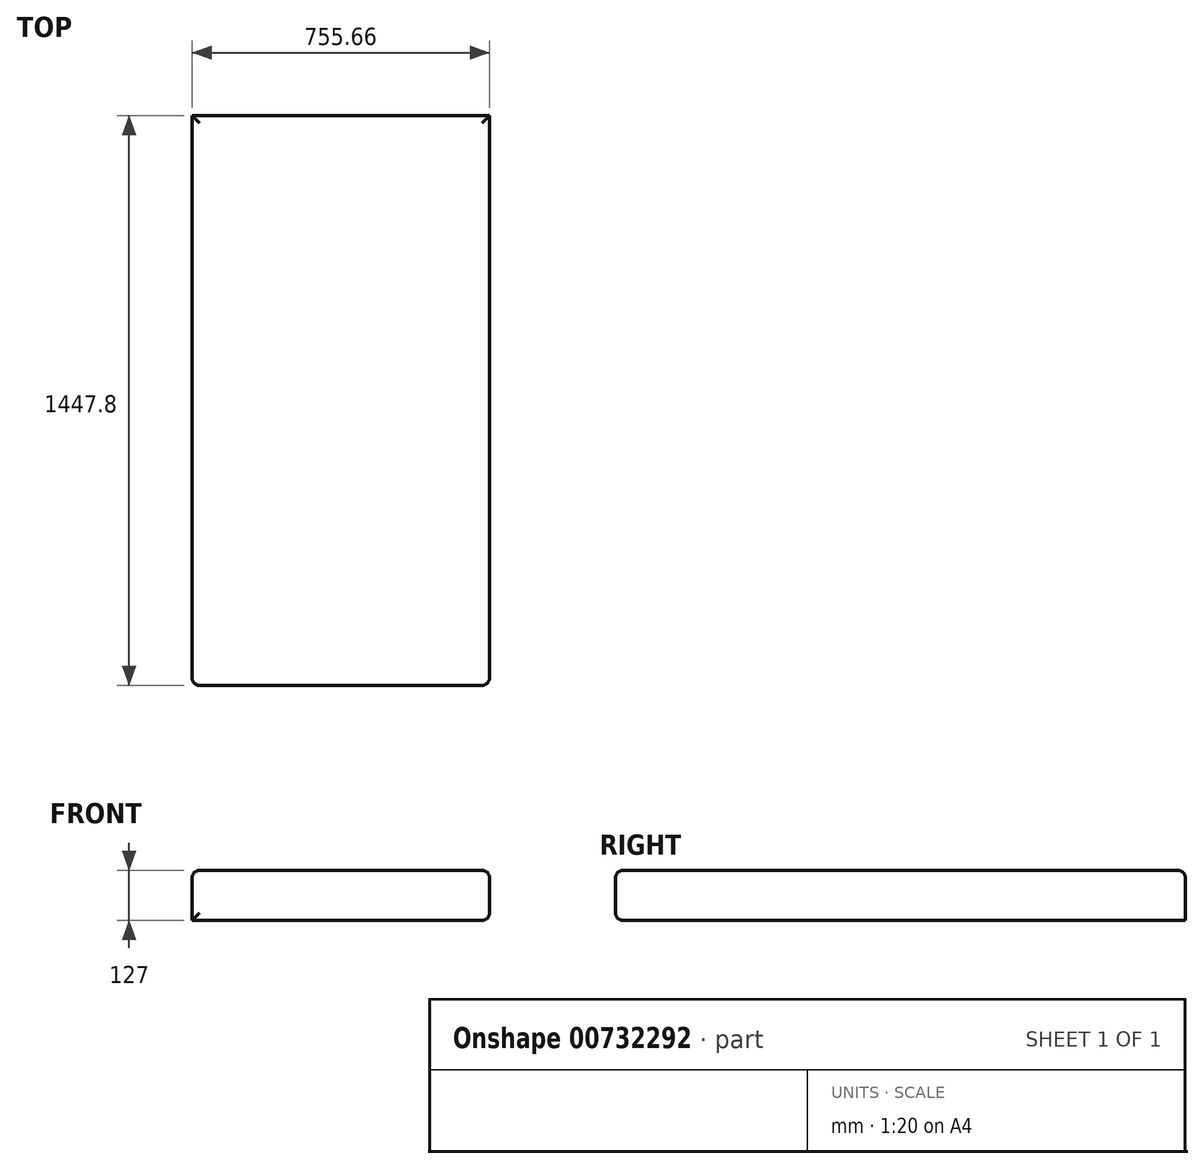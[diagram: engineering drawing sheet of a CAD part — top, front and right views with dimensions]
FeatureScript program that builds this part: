
annotation { "Feature Type Name" : "Feature", "Feature Type Description" : "" }
export const myFeature = defineFeature(function(context is Context, id is Id, definition is map)
    precondition{}
    {
        {
            var Q0;
            Q0=qCreatedBy(makeId("Top.planeOp"),FACE);
            var sketch = newSketch(context, id + "F0", { "sketchPlane" : qUnion([Q0])});
            skLineSegment(sketch, "E0.bottom", {"start": v(377.83, 723.9) * mm, "end": v(-377.83, 723.9) * mm});
            skLineSegment(sketch, "E0.top", {"start": v(377.82, -723.9) * mm, "end": v(-377.83, -723.9) * mm});
            skLineSegment(sketch, "E0.left", {"start": v(377.83, 723.9) * mm, "end": v(377.82, -723.9) * mm});
            skLineSegment(sketch, "E0.right", {"start": v(-377.83, 723.9) * mm, "end": v(-377.83, -723.9) * mm});
            skPoint(sketch, "E0.middle", {"position": v(0, 0) * mm});
            skSolve(sketch);
        }
        {
            var Q0;
            Q0=qSketchRegion(id+"F0",true);
            extrude(context, id + "F1", {"entities" : qUnion([Q0]), "depth" : 127 * mm, "offsetDistance" : 25.4 * mm});
        }
        {
            var Q0;
            Q0=makeQuery(id+"F1.opExtrude","CAP_EDGE",EDGE,{"disambiguationData":[OSD([sQuery(id+"F0.wireOp",EDGE,"E0.right")])],"isStart":false});
            var Q1;
            Q1=makeQuery(id+"F1.opExtrude","CAP_EDGE",EDGE,{"disambiguationData":[OSD([sQuery(id+"F0.wireOp",EDGE,"E0.top")])],"isStart":false});
            var Q2;
            Q2=makeQuery(id+"F1.opExtrude","CAP_EDGE",EDGE,{"disambiguationData":[OSD([sQuery(id+"F0.wireOp",EDGE,"E0.left")])],"isStart":false});
            var Q3;
            Q3=makeQuery(id+"F1.opExtrude","CAP_EDGE",EDGE,{"disambiguationData":[OSD([sQuery(id+"F0.wireOp",EDGE,"E0.bottom")])],"isStart":false});
            var Q4;
            Q4=makeQuery(id+"F1.opExtrude","CAP_EDGE",EDGE,{"disambiguationData":[OSD([sQuery(id+"F0.wireOp",EDGE,"E0.top")])],"isStart":true});
            var Q5;
            Q5=makeQuery(id+"F1.opExtrude","SWEPT_EDGE",EDGE,{"disambiguationData":[OSD([sQuery(id+"F0.wireOp",EDGE,"E0.top"),sQuery(id+"F0.wireOp",EDGE,"E0.left")])]});
            var Q6;
            Q6=makeQuery(id+"F1.opExtrude","SWEPT_EDGE",EDGE,{"disambiguationData":[OSD([sQuery(id+"F0.wireOp",EDGE,"E0.top"),sQuery(id+"F0.wireOp",EDGE,"E0.right")])]});
            var Q7;
            Q7=makeQuery(id+"F1.opExtrude","CAP_EDGE",EDGE,{"disambiguationData":[OSD([sQuery(id+"F0.wireOp",EDGE,"E0.left")])],"isStart":true});
            fillet(context, id + "F2", {"entities" : qUnion([Q0, Q1, Q2, Q3, Q4, Q5, Q6, Q7]), "radius" : 19.05 * mm, "tangentPropagation" : true, "allowEdgeOverflow" : false});
        }
    });
